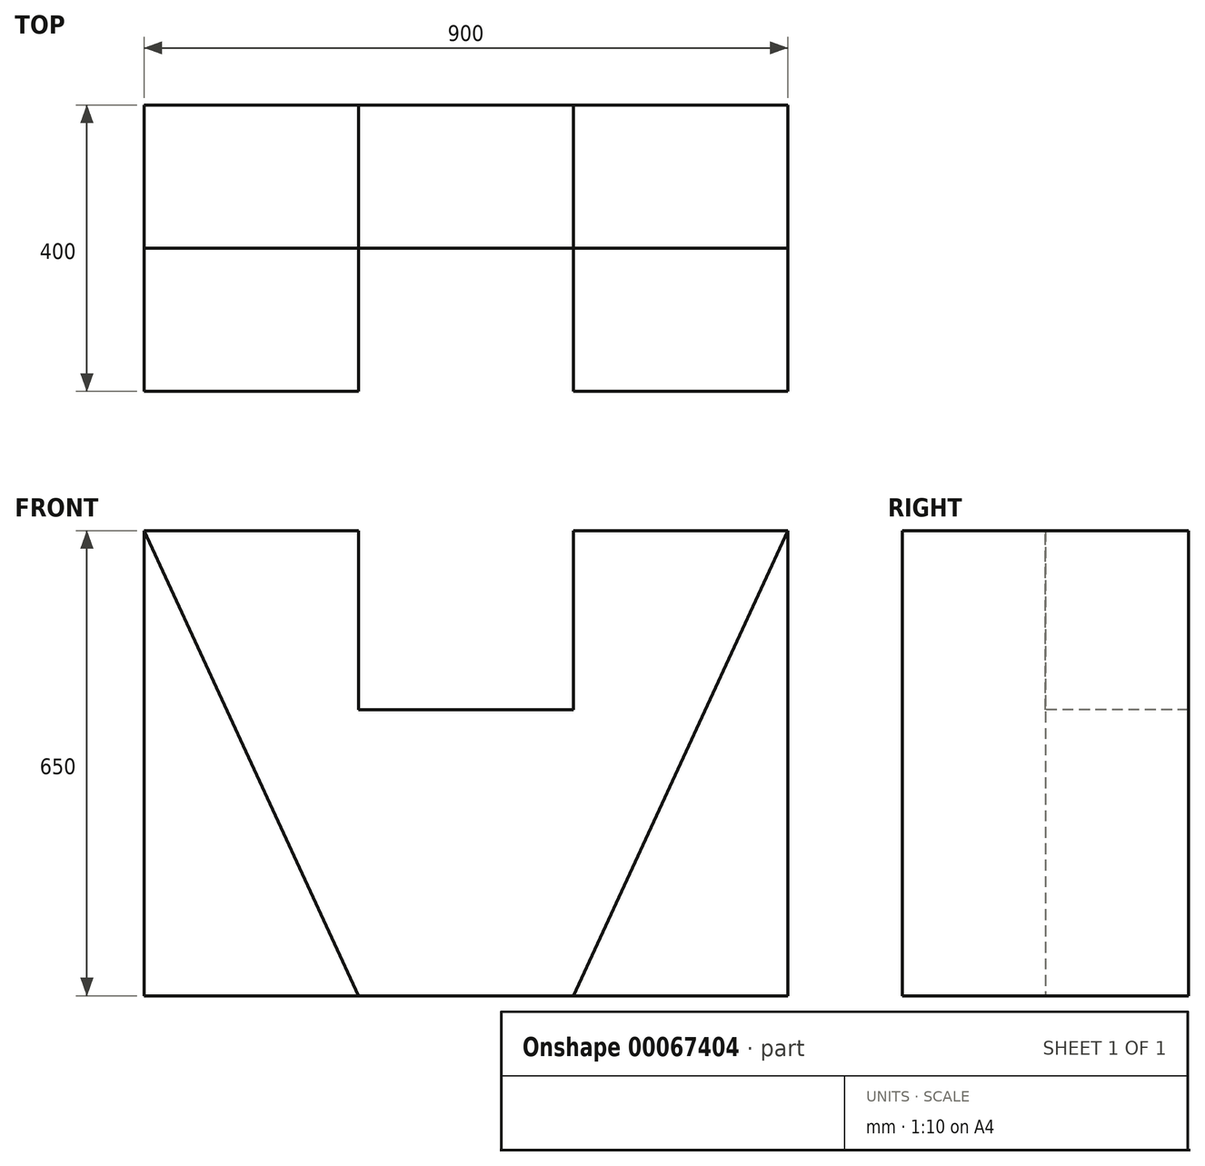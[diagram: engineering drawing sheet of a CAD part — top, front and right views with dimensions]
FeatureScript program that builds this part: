
annotation { "Feature Type Name" : "Feature", "Feature Type Description" : "" }
export const myFeature = defineFeature(function(context is Context, id is Id, definition is map)
    precondition{}
    {
        {
            var Q0;
            Q0=qCreatedBy(makeId("Top.planeOp"),FACE);
            var sketch = newSketch(context, id + "F0", { "sketchPlane" : qUnion([Q0])});
            skLineSegment(sketch, "E0.bottom", {"start": v(450, 200) * mm, "end": v(-450, 200) * mm});
            skLineSegment(sketch, "E0.top", {"start": v(450, -200) * mm, "end": v(-450, -200) * mm});
            skLineSegment(sketch, "E0.left", {"start": v(450, 200) * mm, "end": v(450, -200) * mm});
            skLineSegment(sketch, "E0.right", {"start": v(-450, 200) * mm, "end": v(-450, -200) * mm});
            skPoint(sketch, "E0.middle", {"position": v(0, 0) * mm});
            skSolve(sketch);
        }
        {
            var Q0;
            Q0 = qSketchRegion(id + "F0", true);
            extrude(context, id + "F1", {"entities" : qUnion([Q0]), "depth" : 650 * mm});
        }
        {
            var Q0;
            Q0=makeQuery(id+"F1.opExtrude","SWEPT_FACE",FACE,{"disambiguationData":[OSD([sQuery(id+"F0.wireOp",EDGE,"E0.top")])]});
            var sketch = newSketch(context, id + "F2", { "sketchPlane" : qUnion([Q0])});
            skLineSegment(sketch, "E1", {"start": v(-450, 650) * mm, "end": v(-150, 0) * mm});
            skLineSegment(sketch, "E2", {"start": v(-150, 0) * mm, "end": v(150, 0) * mm});
            skLineSegment(sketch, "E3", {"start": v(150, 0) * mm, "end": v(450, 650) * mm});
            skLineSegment(sketch, "E4", {"start": v(450, 650) * mm, "end": v(-450, 650) * mm});
            skSolve(sketch);
        }
        {
            var Q0;
            Q0 = qSketchRegion(id + "F2", true);
            extrude(context, id + "F3", {"entities" : qUnion([Q0]), "operationType" : NewBodyOperationType.REMOVE, "oppositeDirection" : true, "depth" : 200 * mm});
        }
        {
            var Q0;
            Q0=makeQuery(id+"F3.boolean.opBoolean","COPY",FACE,{"derivedFrom":makeQuery(id+"F3.opExtrude","CAP_FACE",FACE,{"disambiguationData":[OSD([sQuery(id+"F2.wireOp",EDGE,"E1"),sQuery(id+"F2.wireOp",EDGE,"E2"),sQuery(id+"F2.wireOp",EDGE,"E3"),sQuery(id+"F2.wireOp",EDGE,"E4")])],"isStart":false})});
            var sketch = newSketch(context, id + "F4", { "sketchPlane" : qUnion([Q0])});
            skLineSegment(sketch, "E5.bottom", {"start": v(150, 400) * mm, "end": v(-150, 400) * mm});
            skLineSegment(sketch, "E5.top", {"start": v(150, 900) * mm, "end": v(-150, 900) * mm});
            skLineSegment(sketch, "E5.left", {"start": v(150, 400) * mm, "end": v(150, 900) * mm});
            skLineSegment(sketch, "E5.right", {"start": v(-150, 400) * mm, "end": v(-150, 900) * mm});
            skPoint(sketch, "E5.middle", {"position": v(0, 650) * mm});
            skSolve(sketch);
        }
        {
            var Q0;
            Q0 = qSketchRegion(id + "F4", true);
            extrude(context, id + "F5", {"entities" : qUnion([Q0]), "operationType" : NewBodyOperationType.REMOVE, "endBound" : BoundingType.THROUGH_ALL, "oppositeDirection" : true, "depth" : 25 * mm});
        }
    });
